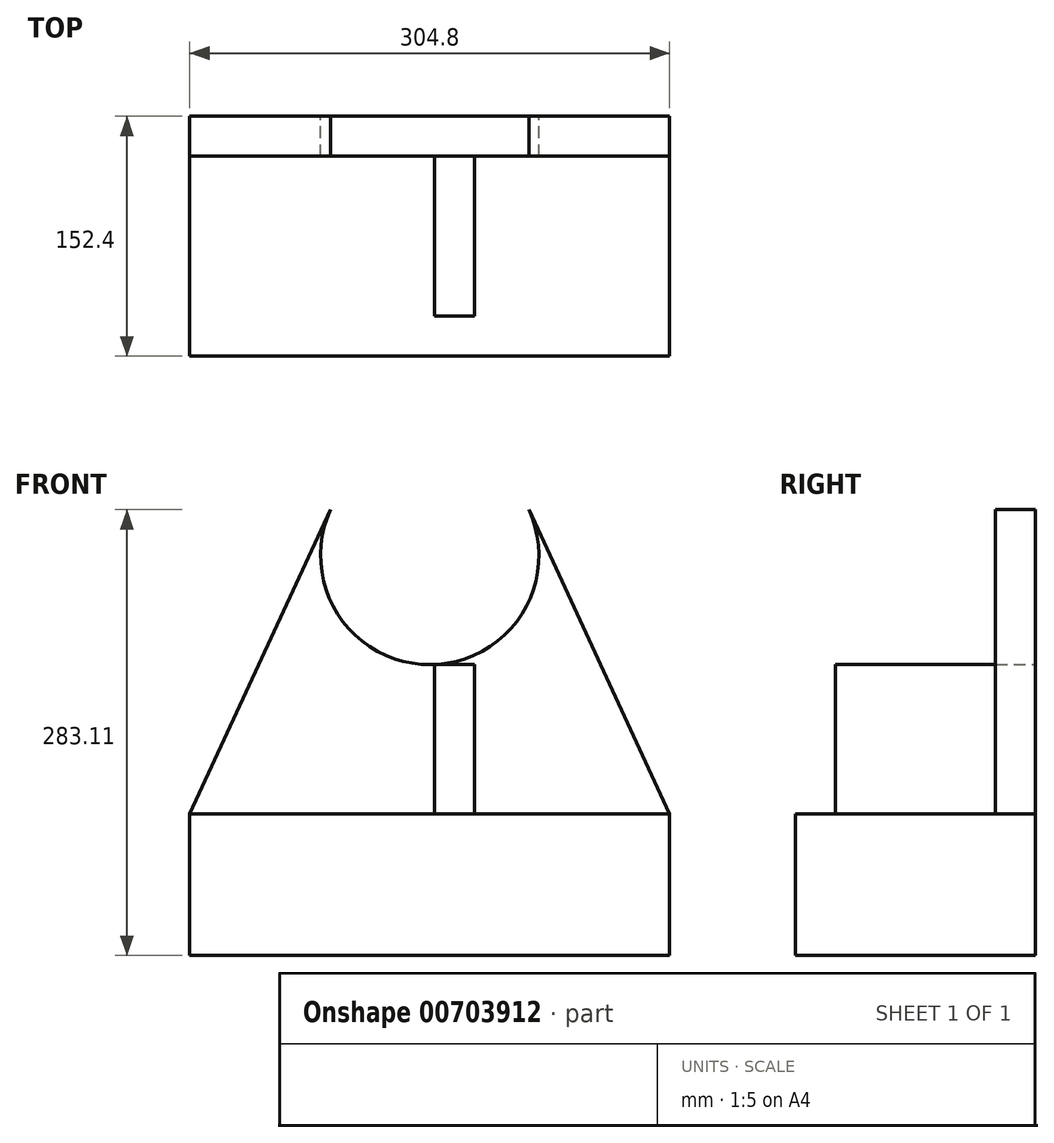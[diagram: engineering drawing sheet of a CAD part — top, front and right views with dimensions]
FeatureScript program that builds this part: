
annotation { "Feature Type Name" : "Feature", "Feature Type Description" : "" }
export const myFeature = defineFeature(function(context is Context, id is Id, definition is map)
    precondition{}
    {
        {
            var Q0;
            Q0=qCreatedBy(makeId("Front.planeOp"),FACE);
            var sketch = newSketch(context, id + "F0", { "sketchPlane" : qUnion([Q0])});
            skLineSegment(sketch, "E0", {"start": v(-168.16, -148.87) * mm, "end": v(136.64, -148.87) * mm});
            skLineSegment(sketch, "E1", {"start": v(-168.16, -148.87) * mm, "end": v(-168.16, -59.18) * mm});
            skLineSegment(sketch, "E2", {"start": v(-168.16, -59.18) * mm, "end": v(-78.7, 134.24) * mm});
            skLineSegment(sketch, "E3", {"start": v(47.19, 134.24) * mm, "end": v(136.64, -59.18) * mm});
            skLineSegment(sketch, "E4", {"start": v(136.64, -59.18) * mm, "end": v(136.64, -148.87) * mm});
            skCircle(sketch, "E5", {"center": v(-15.76, 105.13) * mm, "radius": 69.35 * mm});
            skPoint(sketch, "E5.centerSnap0", {"position": v(-15.76, 85.73) * mm});
            skLineSegment(sketch, "E6", {"start": v(-168.16, -59.18) * mm, "end": v(136.64, -59.18) * mm});
            skCircle(sketch, "E7", {"center": v(-15.76, 105.13) * mm, "radius": 39.07 * mm});
            skSolve(sketch);
        }
        {
            var Q0;
            Q0=makeQuery(id+"F0.imprint","IMPRINT",FACE,{"disambiguationData":[TD([[makeQuery(id+"F0.imprint","IMPRINT",EDGE,{"derivedFrom":sQuery(id+"F0.wireOp",EDGE,"E0")}),1.0]])]});
            extrude(context, id + "F1", {"entities" : qUnion([Q0]), "depth" : 152.4 * mm, "offsetDistance" : 25.4 * mm});
        }
        {
            var Q0;
            {var subQ0=sQuery(id+"F0.wireOp",EDGE,"E2");Q0=makeQuery(id+"F0.imprint","IMPRINT",FACE,{"disambiguationData":[TD([[makeQuery(id+"F0.imprint","IMPRINT",EDGE,{"derivedFrom":subQ0}),-1.0]])]});}
            extrude(context, id + "F2", {"entities" : qUnion([Q0]), "operationType" : NewBodyOperationType.ADD, "depth" : 25.4 * mm, "offsetDistance" : 25.4 * mm});
        }
        {
            var Q0;
            Q0=qCreatedBy(makeId("Right.planeOp"),FACE);
            var sketch = newSketch(context, id + "F3", { "sketchPlane" : qUnion([Q0])});
            skLineSegment(sketch, "E8", {"start": v(-25.4, 35.78) * mm, "end": v(-127.06, 35.78) * mm});
            skLineSegment(sketch, "E9", {"start": v(-127, 35.78) * mm, "end": v(-127, -61.9) * mm});
            skLineSegment(sketch, "E10", {"start": v(-127, -61.9) * mm, "end": v(-23.24, -61.9) * mm});
            skLineSegment(sketch, "E11", {"start": v(-23.24, -61.9) * mm, "end": v(-25.4, 35.78) * mm});
            skSolve(sketch);
        }
        {
            var Q0;
            {var subQ2=sQuery(id+"F3.wireOp",EDGE,"E9");Q0=makeQuery(id+"F3.imprint","IMPRINT",FACE,{"disambiguationData":[TD([[makeQuery(id+"F3.imprint","IMPRINT",EDGE,{"derivedFrom":subQ2}),1.0]])]});}
            extrude(context, id + "F4", {"entities" : qUnion([Q0]), "operationType" : NewBodyOperationType.ADD, "endBound" : BoundingType.SYMMETRIC, "depth" : 25.4 * mm, "offsetDistance" : 25.4 * mm});
        }
    });
